# Revit family: O2.5UMA-NRG (8FT)_18 BF
name_source: partatom
category: Mechanical Equipment
units: mm (PartAtom-declared; Revit-internal decimal feet)

## family parameters
Always vertical = Yes
Cut with Voids When Loaded = No
OmniClass Number = 23.40.40.11.17
OmniClass Title = Refrigerated Cases
Part Type = Normal
Room Calculation Point = No
Round Connector Dimension = Use Radius
Shared = No
Work Plane-Based = Yes

## types (1)
- 08'
    11" BF = Yes
    5" BF = Yes
    ANTI SWEAT APPARENT LOAD = 0 VA
    ANTI SWEAT HEATER AMPS = 0 A
    ANTI SWEAT HEATER WATTAGE = 0 W
    Application Discipline = Dairy/Deli/Produce
    BASE HEIGHT = 5 1/8"
    BLACK WHEELS = <By Category>
    BTU ADD FOR LIGHTS = 1472
    BTU ADD PER SHELF PER FOOT = 92
    BTU PER FOOT CONVENTIONAL = 857
    BTU PER FOOT PARALLEL = 750
    BTUH Conventional = 858
    BTUH Parallel = 750
    CERTIFICATIONS = NSF 7, UL471, CSA
    COIL REFRIGERATION CHARGE = 0.00 lb
    CONTROL TYPE = T-STAT
    CONVENTIONAL EVAPORATOR LOAD = 8328
    CORNICE AND NOSE LIGHT ROWS = 0
    DATE = 07/26/12
    DEDICATED CIRCUIT = YES
    DEFROST AMPS = 0 A
    DEFROST PHASE = 1
    DEFROST TIME AND DURATION = 2 @ 60 MIN
    DEFROST WATTAGE = 0 W
    DIEBOARD HEIGHT = 0"
    DISCHARGE AIR TEMPERATURE = 31 °F
    DRAIN LINE CONNECTION = Drain Connection
    DRAIN LINE DIAMETER = 2"
    DRAIN LINE RADIUS = 1"
    DRAIN PIPE LENGTH = 0"
    DRAIN PIPE TYPE = PVC
    DRIP PAN PLUMB TYPE = HARD
    Default Elevation = 48"
    Defrosts Per Day = 6
    Description = MULTI DECK MERCHANDISER WITH SYNERG-E
    Discharge Air (°F) = 31 °F
    Discharge Air Velocity (FPM) = 180 FPM
    ELECTRIC DEFROST = No
    ELECTRICAL DEFROST VOLTAGE = 0 V
    EQUIPMENT MARK = O2.5UMA-NRG
    EVAPORATOR TEMPERATURE = 28 °F
    Evaporator (°F) = 28 °F
    FAN AMPS = 0 A
    FAN AND ANTI SWEAT HEATER APPARENT LOAD = 38 VA
    FAN APPARENT LOAD = 38 VA
    FAN CONNECTOR DESCRIPTION = FAN AND ANTI SWEAT CONNECTOR
    FAN NUMBER OF POLES = 1
    FAN QUANTITY = 2
    FAN TYPE = ECM
    FAN WATTAGE = 22 W
    Front Sill Height = All
    GROUND FAULT PROTECTION = NO
    HEIGHT = 44 1/8"
    HOT GAS DEFROST = No
    High Efficiency Amps = 0 A
    High Efficiency Watts = 22 W
    High Power (Cornice) Amps = 0 A
    High Power (Cornice) Watts = 30 W
    ISOLATED GROUND REQUIRED = NO
    Keynote = DAIRY/DELI/MEAT/PRODUCE/SEAFOOD
    LED LIGHTING AMPS = 0 A
    LED LIGHTING AMPS PER ROW = 0 A
    LED LIGHTING BTU ADD PER ROW = 36
    LED LIGHTING WATTAGE = 48 W
    LEGEND NUMBER = O2.5UMA-NRG
    LENGTH = 96"
    LENGTH FOR BTU = 8
    LIGHT AMPS = 1 A
    LIGHT TYPE = T8 FLUORESCENT
    LIGHTING APPARENT LOAD = 113 VA
    LIGHTING CONNECTION DESCRIPTION = LIGHTING CONNECTOR
    LIGHTING NUMBER OF POLES = 1
    LIGHTING WATTAGE = 113 VA
    LIQUID LINE CONNECTION = LIQUID LINE CONNECTION
    LIQUID LINE DIAMETER = 0"
    LIQUID LINE RADIUS = 0"
    Light Length = 4'
    Lights Per Row = 2
    Manufacturer = HILL PHOENIX
    Model = O2.5UMA-NRG
    NUMBER OF WIRES = 3
    Number of Fans = 2
    PARALLEL EVAPORATOR LOAD = 7472
    PHASE = 1
    POWER FACTOR = 1
    PRESSURE REGULATOR = 0.00 psi
    RECEPTICAL MOUNTING HEIGHT ABOVE FLOOR = 19 3/4"
    REF PIPE LENGTH = 28 5/8"
    REF PLANE FRONT BACK = 21 5/8"
    REF PLANE LEFT RIGHT = 48"
    REVERSE AIR DEFROST = No
    SET BACK MODE FOR ENERGY CONSERVATION = NO
    SHELF LIGHT ROWS = 2
    SHELVE 1 = Yes
    SHELVE 2 = No
    SHELVE 3 = Yes
    SHELVE LENGTH = 48"
    SIZE OF COLD WATER HOOK UP = 0"
    SIZE OF HOT WATER HOOK-UP = 0"
    SUCTION LINE CONNECTION = SUCTION LINE CONNECTION
    SUCTION LINE DIAMETER = 1"
    SUCTION LINE RADIUS = 0"
    Standard Power Amps = 0 A
    Standard Power Watts = 12 W
    Superheat Set Point @ Bulb (°F) = 6-8
    T8 LIGHT OR LED LIGHT = Yes
    T8 LIGHTING AMPS = 1 A
    T8 LIGHTING AMPS PER ROW = 0 A
    T8 LIGHTING BTU ADD PER ROW = 92
    T8 LIGHTING WATTAGE = 113 W
    TIME OFF DEFROST = Yes
    TOEKICK HEIGHT = 5 1/2"
    TOEKICK INSET = 1 1/2"
    TOTAL APPARENT FAN-LIGHT AND A/S LOAD = 135 VA
    TOTAL CASE AMPS = 1 A
    TOTAL CASE WATTAGE = 135 W
    Timed-Off Defrost Fail-Safe (Min) = 30
    Timed-Off Defrost Termination Temp = 42 °F
    URL = http://www.hillphoenix.com
    VOLTAGE = 120 V
    WATER LINE MOUNTING HEIGHT ABOVE FLOOR = 0"
    WEIGHT = 0.00 lb
    WIDTH = 43 1/4"

## geometry (parser evidence)
native form markers: Blend x2, Sweep x10
no freeform markers — native parametric forms only
